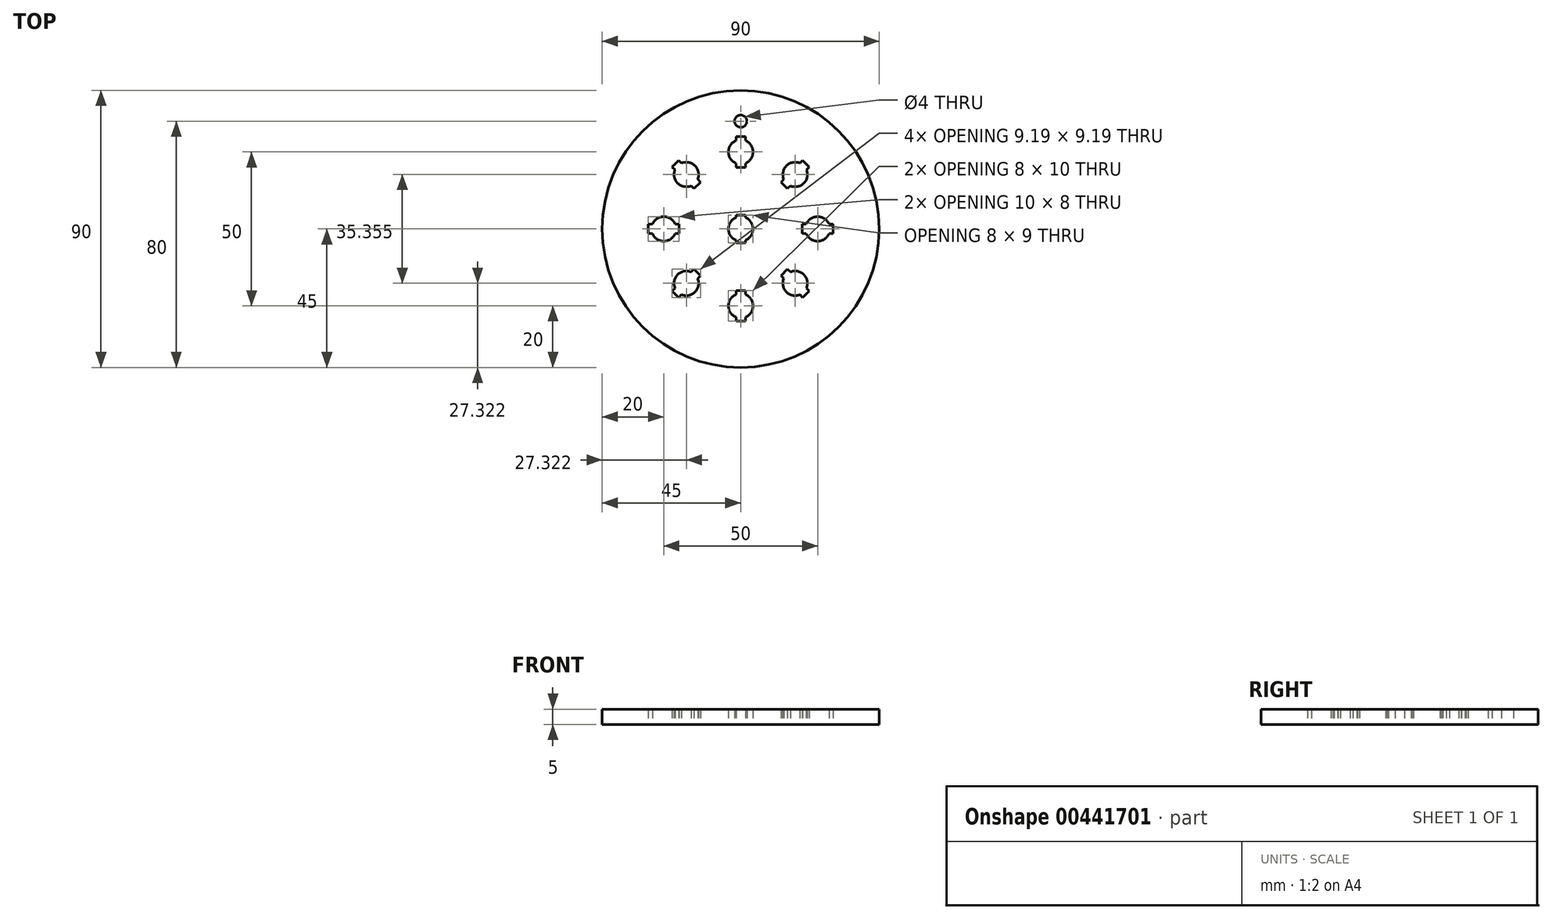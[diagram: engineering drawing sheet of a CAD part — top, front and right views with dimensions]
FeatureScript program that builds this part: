
annotation { "Feature Type Name" : "Feature", "Feature Type Description" : "" }
export const myFeature = defineFeature(function(context is Context, id is Id, definition is map)
    precondition{}
    {
        {
            var Q0;
            Q0=qCreatedBy(makeId("Top.planeOp"),FACE);
            var sketch = newSketch(context, id + "F0", { "sketchPlane" : qUnion([Q0])});
            skCircle(sketch, "E0", {"center": v(0, 0) * mm, "radius": 45 * mm});
            skLineSegment(sketch, "E1", {"start": v(0, 68.18) * mm, "end": v(0, -71.43) * mm, "construction": true});
            skLineSegment(sketch, "E2", {"start": v(-62.18, 0) * mm, "end": v(70.52, 0) * mm, "construction": true});
            skCircle(sketch, "E3", {"center": v(0, 0) * mm, "radius": 4 * mm});
            skCircle(sketch, "E4", {"center": v(0, -25) * mm, "radius": 4 * mm});
            skCircle(sketch, "E5", {"center": v(0, 0) * mm, "radius": 25 * mm, "construction": true});
            skLineSegment(sketch, "E6.bottom", {"start": v(-1.5, -20) * mm, "end": v(1.5, -20) * mm});
            skLineSegment(sketch, "E6.top", {"start": v(-1.5, -30) * mm, "end": v(1.5, -30) * mm});
            skLineSegment(sketch, "E6.left", {"start": v(-1.5, -20) * mm, "end": v(-1.5, -30) * mm});
            skLineSegment(sketch, "E6.right", {"start": v(1.5, -20) * mm, "end": v(1.5, -30) * mm});
            skLineSegment(sketch, "E7", {"start": v(-10.54, -25) * mm, "end": v(14.4, -25) * mm, "construction": true});
            skLineSegment(sketch, "E8.1.0", {"start": v(15.2, -13.08) * mm, "end": v(22.27, -20.15) * mm});
            skCircle(sketch, "E8.1.1", {"center": v(17.68, -17.68) * mm, "radius": 4 * mm});
            skLineSegment(sketch, "E8.1.2", {"start": v(13.08, -15.2) * mm, "end": v(20.15, -22.27) * mm});
            skLineSegment(sketch, "E8.1.3", {"start": v(20.15, -22.27) * mm, "end": v(22.27, -20.15) * mm});
            skLineSegment(sketch, "E8.1.4", {"start": v(13.08, -15.2) * mm, "end": v(15.2, -13.08) * mm});
            skLineSegment(sketch, "E8.2.0", {"start": v(20, 1.5) * mm, "end": v(30, 1.5) * mm});
            skCircle(sketch, "E8.2.1", {"center": v(25, 0) * mm, "radius": 4 * mm});
            skLineSegment(sketch, "E8.2.2", {"start": v(20, -1.5) * mm, "end": v(30, -1.5) * mm});
            skLineSegment(sketch, "E8.2.3", {"start": v(30, -1.5) * mm, "end": v(30, 1.5) * mm});
            skLineSegment(sketch, "E8.2.4", {"start": v(20, -1.5) * mm, "end": v(20, 1.5) * mm});
            skLineSegment(sketch, "E8.3.0", {"start": v(13.08, 15.2) * mm, "end": v(20.15, 22.27) * mm});
            skCircle(sketch, "E8.3.1", {"center": v(17.68, 17.68) * mm, "radius": 4 * mm});
            skLineSegment(sketch, "E8.3.2", {"start": v(15.2, 13.08) * mm, "end": v(22.27, 20.15) * mm});
            skLineSegment(sketch, "E8.3.3", {"start": v(22.27, 20.15) * mm, "end": v(20.15, 22.27) * mm});
            skLineSegment(sketch, "E8.3.4", {"start": v(15.2, 13.08) * mm, "end": v(13.08, 15.2) * mm});
            skLineSegment(sketch, "E8.4.0", {"start": v(-1.5, 20) * mm, "end": v(-1.5, 30) * mm});
            skCircle(sketch, "E8.4.1", {"center": v(0, 25) * mm, "radius": 4 * mm});
            skLineSegment(sketch, "E8.4.2", {"start": v(1.5, 20) * mm, "end": v(1.5, 30) * mm});
            skLineSegment(sketch, "E8.4.3", {"start": v(1.5, 30) * mm, "end": v(-1.5, 30) * mm});
            skLineSegment(sketch, "E8.4.4", {"start": v(1.5, 20) * mm, "end": v(-1.5, 20) * mm});
            skLineSegment(sketch, "E8.5.0", {"start": v(-15.2, 13.08) * mm, "end": v(-22.27, 20.15) * mm});
            skCircle(sketch, "E8.5.1", {"center": v(-17.68, 17.68) * mm, "radius": 4 * mm});
            skLineSegment(sketch, "E8.5.2", {"start": v(-13.08, 15.2) * mm, "end": v(-20.15, 22.27) * mm});
            skLineSegment(sketch, "E8.5.3", {"start": v(-20.15, 22.27) * mm, "end": v(-22.27, 20.15) * mm});
            skLineSegment(sketch, "E8.5.4", {"start": v(-13.08, 15.2) * mm, "end": v(-15.2, 13.08) * mm});
            skLineSegment(sketch, "E8.6.0", {"start": v(-20, -1.5) * mm, "end": v(-30, -1.5) * mm});
            skCircle(sketch, "E8.6.1", {"center": v(-25, 0) * mm, "radius": 4 * mm});
            skLineSegment(sketch, "E8.6.2", {"start": v(-20, 1.5) * mm, "end": v(-30, 1.5) * mm});
            skLineSegment(sketch, "E8.6.3", {"start": v(-30, 1.5) * mm, "end": v(-30, -1.5) * mm});
            skLineSegment(sketch, "E8.6.4", {"start": v(-20, 1.5) * mm, "end": v(-20, -1.5) * mm});
            skLineSegment(sketch, "E8.7.0", {"start": v(-13.08, -15.2) * mm, "end": v(-20.15, -22.27) * mm});
            skCircle(sketch, "E8.7.1", {"center": v(-17.68, -17.68) * mm, "radius": 4 * mm});
            skLineSegment(sketch, "E8.7.2", {"start": v(-15.2, -13.08) * mm, "end": v(-22.27, -20.15) * mm});
            skLineSegment(sketch, "E8.7.3", {"start": v(-22.27, -20.15) * mm, "end": v(-20.15, -22.27) * mm});
            skLineSegment(sketch, "E8.7.4", {"start": v(-15.2, -13.08) * mm, "end": v(-13.08, -15.2) * mm});
            skCircle(sketch, "E9", {"center": v(0, 35) * mm, "radius": 2 * mm});
            skLineSegment(sketch, "E10.bottom", {"start": v(-1.5, 4.5) * mm, "end": v(1.5, 4.5) * mm});
            skLineSegment(sketch, "E10.top", {"start": v(-1.5, -4.5) * mm, "end": v(1.5, -4.5) * mm});
            skLineSegment(sketch, "E10.left", {"start": v(-1.5, 4.5) * mm, "end": v(-1.5, -4.5) * mm});
            skLineSegment(sketch, "E10.right", {"start": v(1.5, 4.5) * mm, "end": v(1.5, -4.5) * mm});
            skSolve(sketch);
        }
        {
            var Q0;
            Q0 = qSketchRegion(id + "F0", true);
            extrude(context, id + "F1", {"entities" : qUnion([Q0]), "endBound" : BoundingType.SYMMETRIC, "depth" : 5 * mm});
        }
    });
